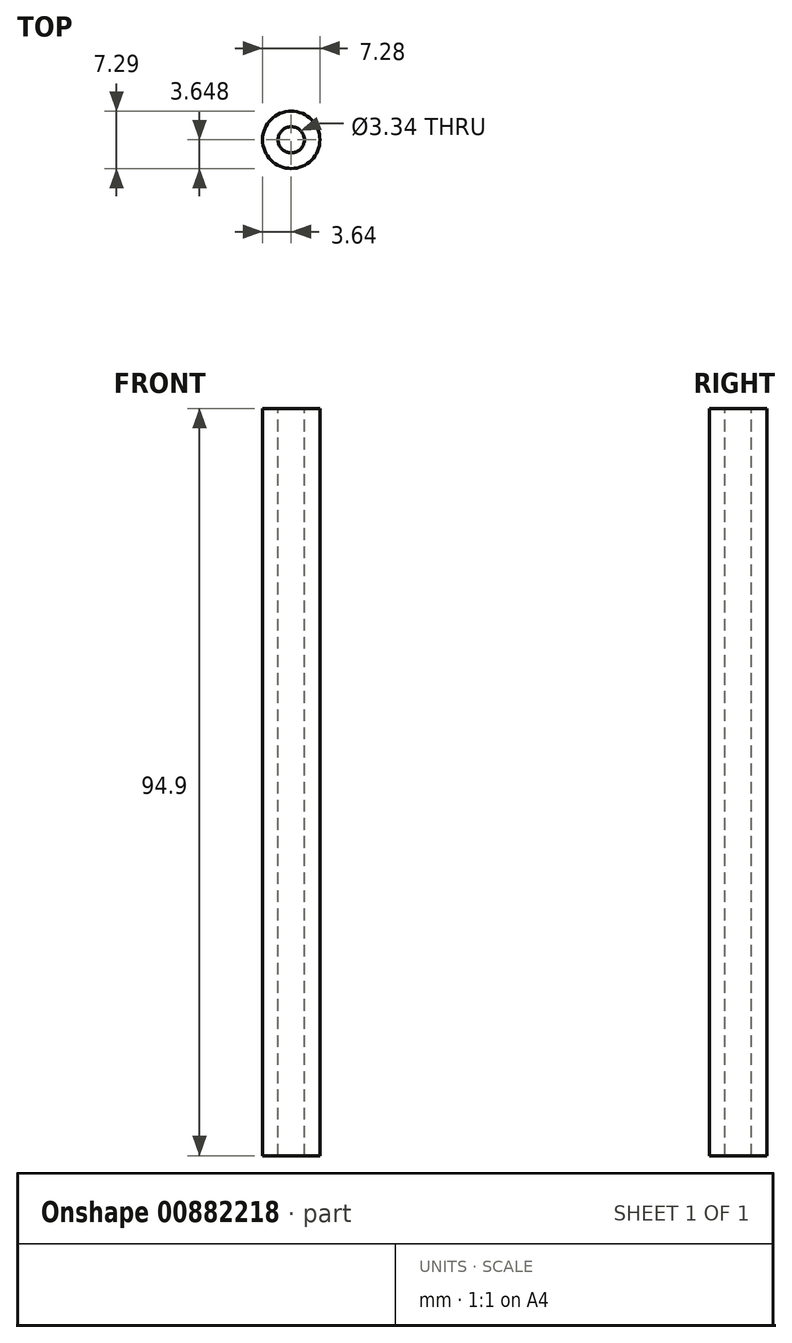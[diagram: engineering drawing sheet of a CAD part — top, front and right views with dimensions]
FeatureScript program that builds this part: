
annotation { "Feature Type Name" : "Feature", "Feature Type Description" : "" }
export const myFeature = defineFeature(function(context is Context, id is Id, definition is map)
    precondition{}
    {
        {
            var Q0;
            Q0=qCreatedBy(makeId("Right.planeOp"),FACE);
            var sketch = newSketch(context, id + "F0", { "sketchPlane" : qUnion([Q0])});
            skLineSegment(sketch, "E0", {"start": v(-24.67, 45.12) * mm, "end": v(-24.67, -49.78) * mm});
            skLineSegment(sketch, "E1", {"start": v(-22.7, 43.14) * mm, "end": v(-22.7, -49.78) * mm});
            skLineSegment(sketch, "E2", {"start": v(-24.67, 45.12) * mm, "end": v(-22.7, 45.12) * mm});
            skLineSegment(sketch, "E3", {"start": v(-22.7, 45.12) * mm, "end": v(-22.7, 43.14) * mm});
            skLineSegment(sketch, "E4", {"start": v(-22.7, -49.78) * mm, "end": v(-24.67, -49.78) * mm});
            skLineSegment(sketch, "E5", {"start": v(-21.02, 45.47) * mm, "end": v(-21.02, 42.6) * mm});
            skSolve(sketch);
        }
        {
            var Q0;
            Q0 = qSketchRegion(id + "F0", true);
            var Q1;
            Q1=sQuery(id+"F0.wireOp",EDGE,"E5");
            revolve(context, id + "F1", {"surfaceOperationType" : NewSurfaceOperationType.NEW, "entities" : qUnion([Q0]), "axis" : qUnion([Q1]), "revolveType" : RevolveType.FULL});
        }
    });
